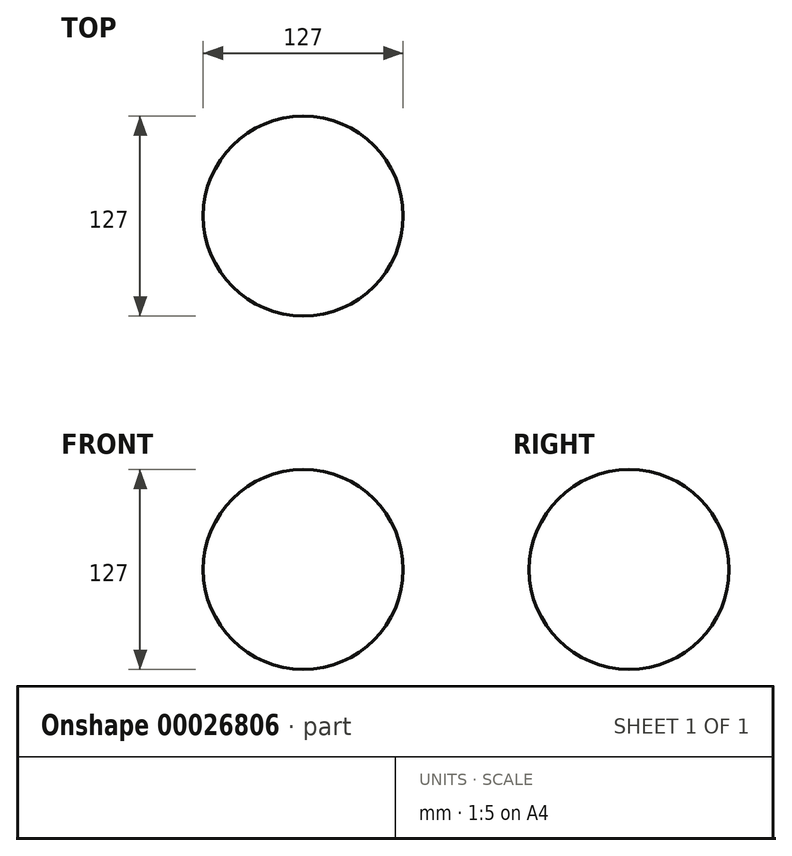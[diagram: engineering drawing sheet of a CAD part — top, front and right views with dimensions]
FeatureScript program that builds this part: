
annotation { "Feature Type Name" : "Feature", "Feature Type Description" : "" }
export const myFeature = defineFeature(function(context is Context, id is Id, definition is map)
    precondition{}
    {
        {
            var Q0;
            Q0=qCreatedBy(makeId("Front.planeOp"),FACE);
            var sketch = newSketch(context, id + "F0", { "sketchPlane" : qUnion([Q0])});
            skArc(sketch, "E0", {"start": v(-20.12, -59.78) * mm, "mid": v(43.38, 3.72) * mm, "end": v(-20.12, 67.22) * mm});
            skLineSegment(sketch, "E1", {"start": v(-20.12, 67.22) * mm, "end": v(-20.12, -59.78) * mm});
            skSolve(sketch);
        }
        {
            var Q0;
            Q0=makeQuery(id+"F0.imprint","IMPRINT",FACE,{"disambiguationData":[TD([[makeQuery(id+"F0.imprint","IMPRINT",EDGE,{"derivedFrom":sQuery(id+"F0.wireOp",EDGE,"E0")}),1.0]])]});
            var Q1;
            Q1=sQuery(id+"F0.wireOp",EDGE,"E1");
            revolve(context, id + "F1", {"entities" : qUnion([Q0]), "axis" : qUnion([Q1]), "revolveType" : RevolveType.FULL});
        }
    });
